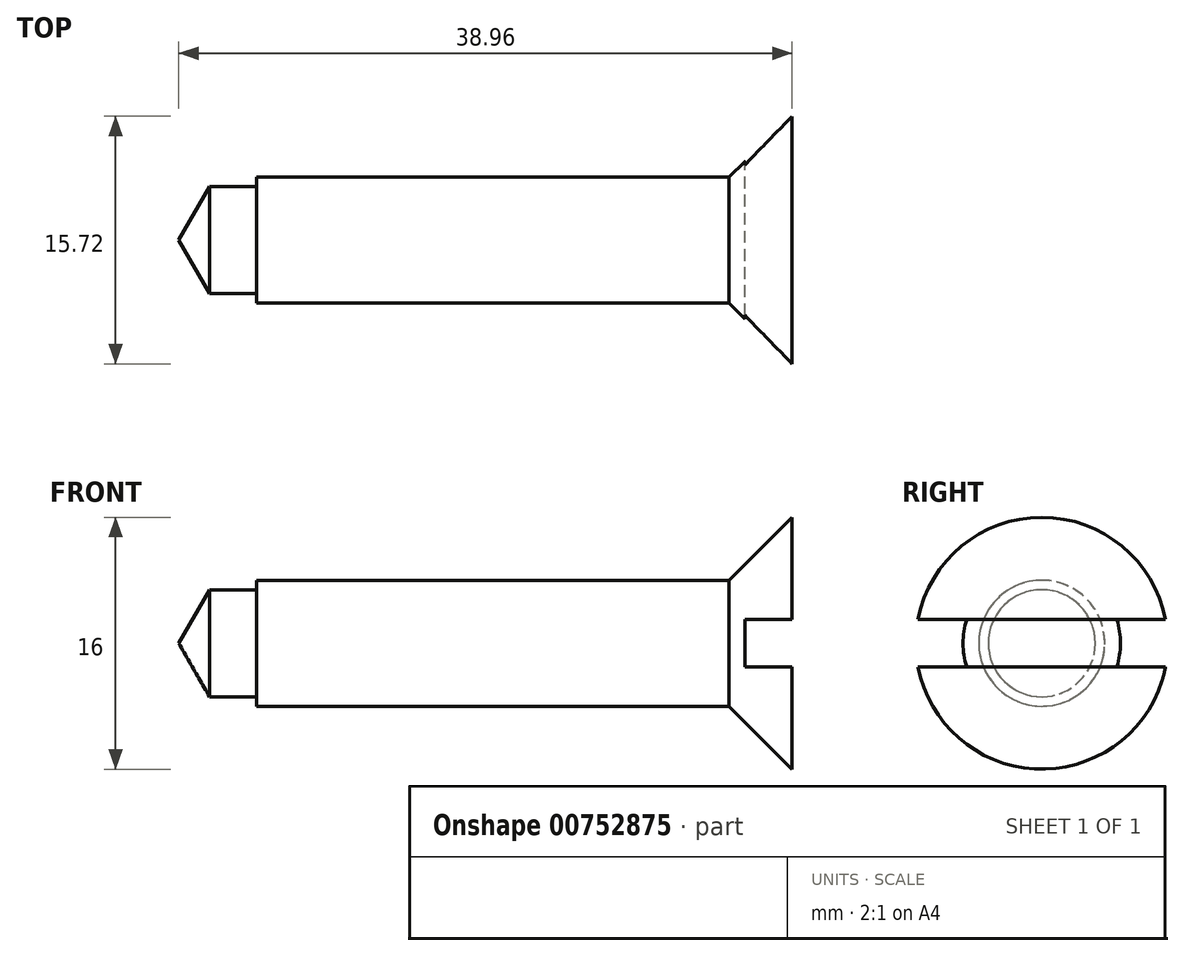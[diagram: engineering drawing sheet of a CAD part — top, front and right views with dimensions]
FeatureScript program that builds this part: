
annotation { "Feature Type Name" : "Feature", "Feature Type Description" : "" }
export const myFeature = defineFeature(function(context is Context, id is Id, definition is map)
    precondition{}
    {
        {
            var Q0;
            Q0=qCreatedBy(makeId("Front.planeOp"),FACE);
            var sketch = newSketch(context, id + "F0", { "sketchPlane" : qUnion([Q0])});
            skLineSegment(sketch, "E0", {"start": v(-41, 0) * mm, "end": v(60.43, 0) * mm});
            skLineSegment(sketch, "E1", {"start": v(38.96, 0) * mm, "end": v(38.96, 8) * mm});
            skLineSegment(sketch, "E2", {"start": v(38.96, 8) * mm, "end": v(34.96, 4) * mm});
            skLineSegment(sketch, "E3", {"start": v(34.96, 4) * mm, "end": v(34.96, 0) * mm});
            skLineSegment(sketch, "E4", {"start": v(34.96, 4) * mm, "end": v(4.96, 4) * mm});
            skLineSegment(sketch, "E5", {"start": v(4.96, 4) * mm, "end": v(4.96, 0) * mm});
            skLineSegment(sketch, "E6", {"start": v(4.96, 3.4) * mm, "end": v(1.96, 3.4) * mm});
            skLineSegment(sketch, "E7", {"start": v(1.96, 3.4) * mm, "end": v(0, 0) * mm});
            skSolve(sketch);
        }
        {
            var Q0;
            {var subQ0=sQuery(id+"F0.wireOp",EDGE,"E1");Q0=makeQuery(id+"F0.imprint","IMPRINT",FACE,{"disambiguationData":[TD([[makeQuery(id+"F0.imprint","IMPRINT",EDGE,{"derivedFrom":subQ0}),1.0]])]});}
            var Q1;
            {var subQ3=sQuery(id+"F0.wireOp",EDGE,"E3");Q1=makeQuery(id+"F0.imprint","IMPRINT",FACE,{"disambiguationData":[TD([[makeQuery(id+"F0.imprint","IMPRINT",EDGE,{"derivedFrom":subQ3}),-1.0]])]});}
            var Q2;
            {var subQ4=sQuery(id+"F0.wireOp",EDGE,"E6");Q2=makeQuery(id+"F0.imprint","IMPRINT",FACE,{"disambiguationData":[TD([[makeQuery(id+"F0.imprint","IMPRINT",EDGE,{"derivedFrom":subQ4}),1.0]])]});}
            var Q3;
            Q3=sQuery(id+"F0.wireOp",EDGE,"E0");
            revolve(context, id + "F1", {"surfaceOperationType" : NewSurfaceOperationType.NEW, "entities" : qUnion([Q0, Q1, Q2]), "axis" : qUnion([Q3]), "revolveType" : RevolveType.FULL});
        }
        {
            var Q0;
            Q0=makeQuery(id+"F1.opRevolve","SWEPT_FACE",FACE,{"disambiguationData":[OSD([sQuery(id+"F0.wireOp",EDGE,"E1")])]});
            var sketch = newSketch(context, id + "F2", { "sketchPlane" : qUnion([Q0])});
            skLineSegment(sketch, "E8.bottom", {"start": v(-10.8, 1.5) * mm, "end": v(10.2, 1.5) * mm});
            skLineSegment(sketch, "E8.top", {"start": v(-10.8, -1.5) * mm, "end": v(10.2, -1.5) * mm});
            skLineSegment(sketch, "E8.left", {"start": v(-10.8, 1.5) * mm, "end": v(-10.8, -1.5) * mm});
            skLineSegment(sketch, "E8.right", {"start": v(10.2, 1.5) * mm, "end": v(10.2, -1.5) * mm});
            skSolve(sketch);
        }
        {
            var Q0;
            {var subQ0=sQuery(id+"F2.wireOp",EDGE,"E8.bottom");var subQ1=makeQuery(id+"F1.opRevolve","SWEPT_EDGE",EDGE,{"disambiguationData":[OSD([sQuery(id+"F0.wireOp",EDGE,"E1"),sQuery(id+"F0.wireOp",EDGE,"E2")])]});var subQ2=makeQuery(id+"F2.imprint","INTERSECT",VERTEX,{"disambiguationData":[OD(0.0)],"derivedFrom":[subQ1,subQ0]});Q0=makeQuery(id+"F2.imprint","IMPRINT",FACE,{"disambiguationData":[TD([[makeQuery(id+"F2.imprint","IMPRINT",EDGE,{"disambiguationData":[TD([[subQ2,-1.0]])],"derivedFrom":subQ0}),-1.0]])]});}
            extrude(context, id + "F3", {"entities" : qUnion([Q0]), "operationType" : NewBodyOperationType.REMOVE, "oppositeDirection" : true, "depth" : 3 * mm, "offsetDistance" : 25 * mm});
        }
    });
